# Revit family: 600х1200
name_source: partatom
category: Обобщенные модели
units: mm (PartAtom-declared; Revit-internal decimal feet)

## family parameters
Всегда вертикально = Да
Может служить основой для арматурных стержней = Нет
На основе рабочей плоскости = Нет
Общий = Нет
При загрузке вырезать с полостями = Нет
Размер круглого соединителя = Использовать диаметр
Тип детали = Нормальный
Точка расчета площади = Нет

## types (12) — shared parameters
ADSK_URL страницы изделия = https://www.ssd.ru
ADSK_Единица измерения = шт
ADSK_Завод-изготовитель = АО СВЯЗЬСТРОЙДЕТАЛЬ
Материал колес и ручек = Металл белый
zero-valued in all types: Ноль

## per-type parameters (varying)
| type | ADSK_Код изделия | ADSK_Масса_Текст | ADSK_Наименование | ADSK_Размер_Высота | Двустворчатая дверь | Материал каркаса | Материал крепежей | Не двустворчатая дверь | Описание |
| ШТ-НП-С-33U-600-1200-ПП-Ч | 130411-01422 | 91.0 | Шкаф телекоммуникационный напольный серверный 19&quot;. 33U(600x1200) . ШТ-НП-С-33U-600-1200-ПП-Ч передняя перф. задняя перф. черн. | 1667 мм | Нет | Металл черный | Металл черный | Да | Шкаф телекоммуникационный напольный серверный 19&quot;. 33U(600x1200) . ШТ-НП-С-33U-600-1200-ПП-Ч передняя перф. задняя перф. черн. |
| ШТ-НП-С-33U-600-1200-П2П-Ч | 130411-01423 | 91.0 | Шкаф телекоммуникационный напольный серверный 19&quot;. 33U(600x1200) . ШТ-НП-С-33U-600-1200-П2П-Ч передняя перф. задняя двустворчатая перф. черн. | 1667 мм | Да | Металл черный | Металл черный | Нет | Шкаф телекоммуникационный напольный серверный 19&quot;. 33U(600x1200) . ШТ-НП-С-33U-600-1200-П2П-Ч передняя перф. задняя двустворчатая перф. черн. |
| ШТ-НП-С-42U-600-1200-ПП-Ч | 130411-01424 | 92.0 | Шкаф телекоммуникационный напольный серверный 19&quot;.42U(600x1200) . ШТ-НП-С-42U-600-1200-ПП-Ч передняя и задняя дверь перфорированная черн. | 2067 мм | Нет | Металл черный | Металл черный | Да | Шкаф телекоммуникационный напольный серверный 19&quot;.42U(600x1200) . ШТ-НП-С-42U-600-1200-ПП-Ч передняя и задняя дверь перфорированная черн. |
| ШТ-НП-С-42U-600-1200-П2П-Ч | 130411-01263 | 92.0 | Шкаф телекоммуникационный напольный серверный 19&quot;.42U(600x1200) . ШТ-НП-С-42U-600-1200-П2П-Ч передняя перф. задняя двустворчатая перф. черн. | 2067 мм | Да | Металл черный | Металл черный | Нет | Шкаф телекоммуникационный напольный серверный 19&quot;.42U(600x1200) . ШТ-НП-С-42U-600-1200-П2П-Ч передняя перф. задняя двустворчатая перф. черн. |
| ШТ-НП-С-47U-600-1200-ПП-Ч | 130411-01425 | 110.0 | Шкаф телекоммуникационный напольный серверный 19&quot;.47U(600x1200) . ШТ-НП-С-47U-600-1200-ПП-Ч передняя и задняя дверь перфорированная черн. | 2289 мм | Нет | Металл черный | Металл черный | Да | Шкаф телекоммуникационный напольный серверный 19&quot;.47U(600x1200) . ШТ-НП-С-47U-600-1200-ПП-Ч передняя и задняя дверь перфорированная черн. |
| ШТ-НП-С-47U-600-1200-П2П-Ч | 130411-01426 | 110.0 | Шкаф телекоммуникационный напольный серверный 19&quot;. 47U(600x1200) . ШТ-НП-С-47U-600-1200-П2П-Ч передняя перф. задняя двустворчатая перф. черн. | 2289 мм | Да | Металл черный | Металл черный | Нет | Шкаф телекоммуникационный напольный серверный 19&quot;. 47U(600x1200) . ШТ-НП-С-47U-600-1200-П2П-Ч передняя перф. задняя двустворчатая перф. черн. |
| ШТ-НП-С-33U-600-1200-ПП | 130411-00921 | 91.0 | Шкаф телекоммуникационный напольный серверный 19&quot;.33U(600x1200) . ШТ-НП-С-33U-600-1200-ПП передняя.задняя двери перфорированные ССД | 1667 мм | Нет | Металл | Металл | Да | Шкаф телекоммуникационный напольный серверный 19&quot;.33U(600x1200) . ШТ-НП-С-33U-600-1200-ПП передняя.задняя двери перфорированные ССД |
| ШТ-НП-С-33U-600-1200-П2П | 130411-00922 | 91.0 | Шкаф телекоммуникационный напольный серверный 19&quot;.33U(600x1200) . ШТ-НП-С-33U-600-1200-П2П передняя дверь перфорипрованная.задняя перф.двойная. ССД | 1667 мм | Да | Металл | Металл | Нет | Шкаф телекоммуникационный напольный серверный 19&quot;.33U(600x1200) . ШТ-НП-С-33U-600-1200-П2П передняя дверь перфорипрованная.задняя перф.двойная. ССД |
| ШТ-НП-С-42U-600-1200-ПП | 130411-00923 | 92.0 | Шкаф телекоммуникационный напольный серверный 19&quot;.42U(600x1200) . ШТ-НП-С-42U-600-1200-ПП передняя.задняя двери перфорированные ССД | 2067 мм | Нет | Металл | Металл | Да | Шкаф телекоммуникационный напольный серверный 19&quot;.42U(600x1200) . ШТ-НП-С-42U-600-1200-ПП передняя.задняя двери перфорированные ССД |
| ШТ-НП-С-42U-600-1200-П2П | 130411-00924 | 92.0 | Шкаф телекоммуникационный напольный серверный 19&quot;.42U(600x1200) . ШТ-НП-С-42U-600-1200-П2П передняя дверь перфорированная.задняя перф.двойная. ССД | 2067 мм | Да | Металл | Металл | Нет | Шкаф телекоммуникационный напольный серверный 19&quot;.42U(600x1200) . ШТ-НП-С-42U-600-1200-П2П передняя дверь перфорированная.задняя перф.двойная. ССД |
| ШТ-НП-С-47U-600-1200-ПП | 130411-00925 | 110.0 | Шкаф телекоммуникационный напольный серверный 19&quot;.47U(600x1200) . ШТ-НП-С-47U-600-1200-ПП передняя.задняя двери перфорированные ССД | 2289 мм | Нет | Металл | Металл | Да | Шкаф телекоммуникационный напольный серверный 19&quot;.47U(600x1200) . ШТ-НП-С-47U-600-1200-ПП передняя.задняя двери перфорированные ССД |
| ШТ-НП-С-47U-600-1200-П2П | 130411-00926 | 110.0 | Шкаф телекоммуникационный напольный серверный 19&quot;.47U(600x1200) . ШТ-НП-С-47U-600-1200-П2П передняя дверь перфорипрованная.задняя перф.двойная. ССД | 2289 мм | Да | Металл | Металл | Нет | Шкаф телекоммуникационный напольный серверный 19&quot;.47U(600x1200) . ШТ-НП-С-47U-600-1200-П2П передняя дверь перфорипрованная.задняя перф.двойная. ССД |

note: column(s) folded — value = type name in every type: ADSK_Наименование краткое

## geometry (parser evidence)
native form markers: Blend x4
no freeform markers — native parametric forms only
